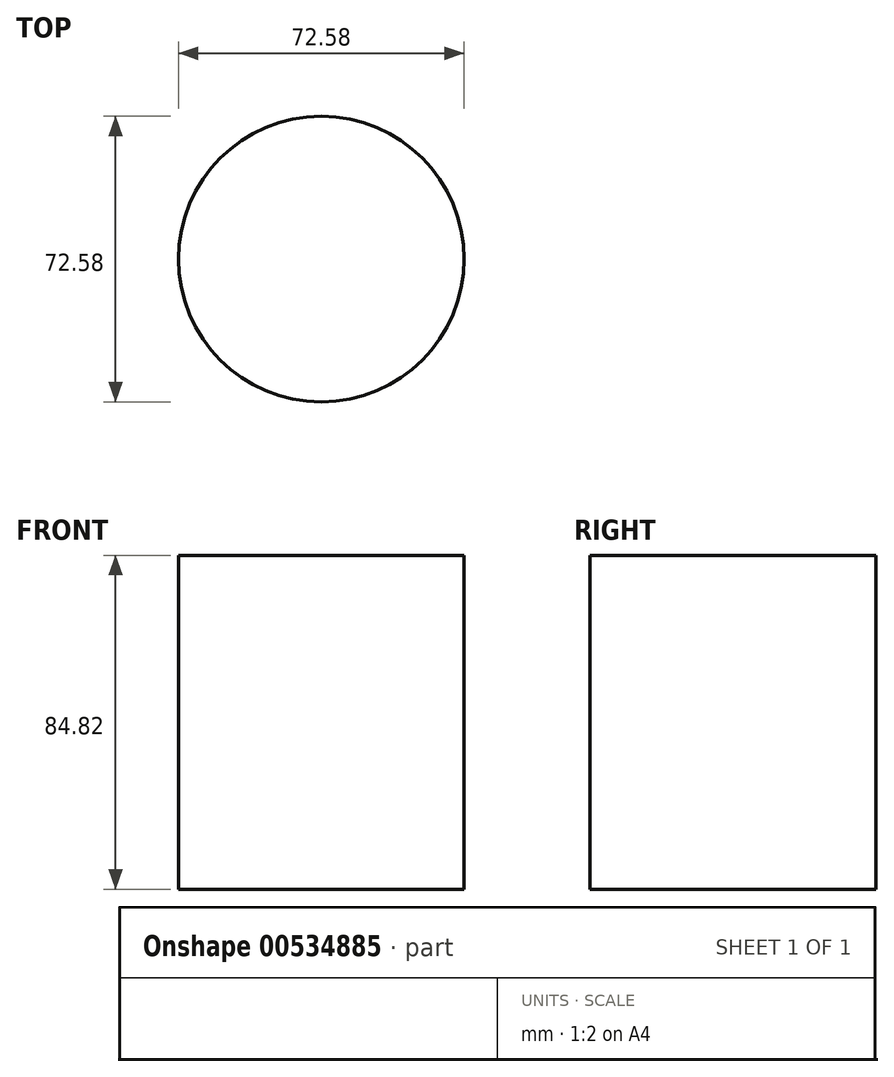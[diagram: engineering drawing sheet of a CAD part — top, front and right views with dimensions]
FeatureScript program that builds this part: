
annotation { "Feature Type Name" : "Feature", "Feature Type Description" : "" }
export const myFeature = defineFeature(function(context is Context, id is Id, definition is map)
    precondition{}
    {
        {
            var Q0;
            Q0=qCreatedBy(makeId("Top.planeOp"),FACE);
            var sketch = newSketch(context, id + "F0", { "sketchPlane" : qUnion([Q0])});
            skCircle(sketch, "E0", {"center": v(19.47, 30.62) * mm, "radius": 36.29 * mm});
            skPoint(sketch, "E0.first.point", {"position": v(41.62, 59.37) * mm});
            skPoint(sketch, "E0.second.point", {"position": v(-16.76, 28.62) * mm});
            skPoint(sketch, "E0.third.point", {"position": v(0, 0) * mm});
            skSolve(sketch);
        }
        {
            var Q0;
            Q0 = qSketchRegion(id + "F0", true);
            extrude(context, id + "F1", {"entities" : qUnion([Q0]), "depth" : 84.82 * mm, "offsetDistance" : 25.4 * mm});
        }
    });
